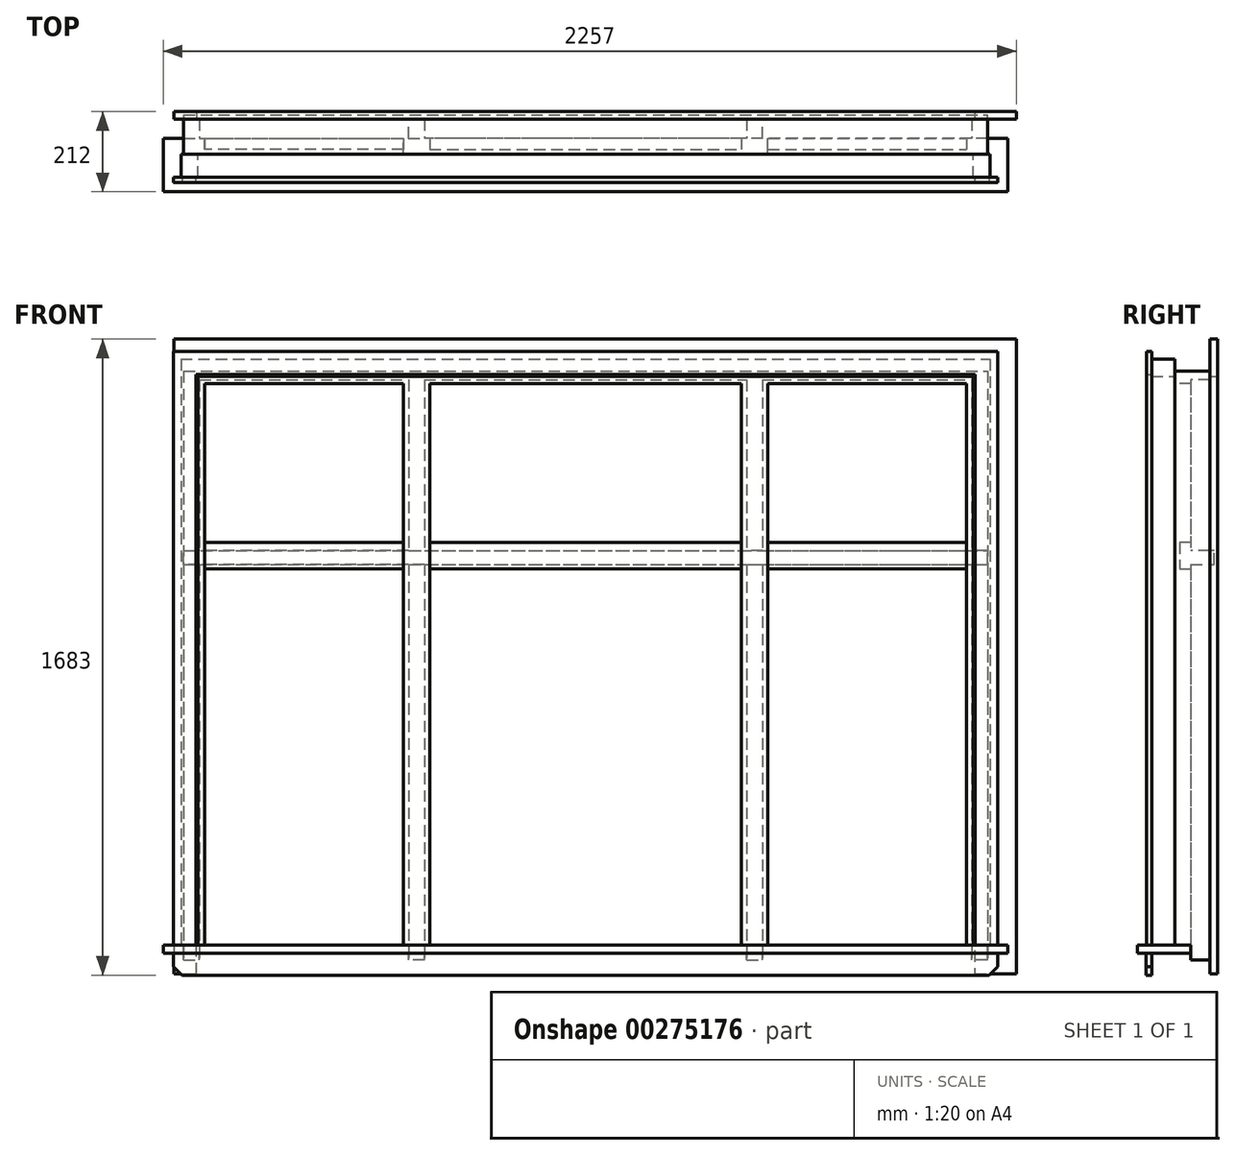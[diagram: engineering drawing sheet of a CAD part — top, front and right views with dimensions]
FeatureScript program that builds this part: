
annotation { "Feature Type Name" : "Feature", "Feature Type Description" : "" }
export const myFeature = defineFeature(function(context is Context, id is Id, definition is map)
    precondition{}
    {
        {
            var Q0;
            Q0=qCreatedBy(makeId("Top.planeOp"),FACE);
            var sketch = newSketch(context, id + "F0", { "sketchPlane" : qUnion([Q0])});
            skLineSegment(sketch, "E0", {"start": v(426.5, 0) * mm, "end": v(412.5, 0) * mm});
            skLineSegment(sketch, "E1", {"start": v(412.5, 0) * mm, "end": v(412.5, -42) * mm});
            skLineSegment(sketch, "E2", {"start": v(412.5, -42) * mm, "end": v(482.5, -42) * mm});
            skLineSegment(sketch, "E3", {"start": v(482.5, -42) * mm, "end": v(482.5, 0) * mm});
            skLineSegment(sketch, "E4", {"start": v(482.5, 0) * mm, "end": v(468.5, 0) * mm});
            skLineSegment(sketch, "E5", {"start": v(468.5, 0) * mm, "end": v(468.5, 50) * mm});
            skLineSegment(sketch, "E6", {"start": v(468.5, 50) * mm, "end": v(426.5, 50) * mm});
            skLineSegment(sketch, "E7", {"start": v(426.5, 50) * mm, "end": v(426.5, 0) * mm});
            skLineSegment(sketch, "E8", {"start": v(1007.5, 0) * mm, "end": v(1007.5, -42) * mm});
            skLineSegment(sketch, "E9", {"start": v(1007.5, -42) * mm, "end": v(1063.5, -42) * mm});
            skLineSegment(sketch, "E10", {"start": v(1063.5, -42) * mm, "end": v(1063.5, 50) * mm});
            skLineSegment(sketch, "E11", {"start": v(1063.5, 50) * mm, "end": v(1021.5, 50) * mm});
            skLineSegment(sketch, "E12", {"start": v(1021.5, 50) * mm, "end": v(1021.5, 0) * mm});
            skLineSegment(sketch, "E13", {"start": v(1021.5, 0) * mm, "end": v(1007.5, 0) * mm});
            skSolve(sketch);
        }
        {
            var Q0;
            Q0 = qSketchRegion(id + "F0", true);
            extrude(context, id + "F1", {"entities" : qUnion([Q0]), "depth" : 1485 * mm});
        }
        {
            var Q0;
            Q0=makeQuery(id+"F1.opExtrude","CAP_FACE",FACE,{"disambiguationData":[OSD([sQuery(id+"F0.wireOp",EDGE,"E8"),sQuery(id+"F0.wireOp",EDGE,"E9"),sQuery(id+"F0.wireOp",EDGE,"E10"),sQuery(id+"F0.wireOp",EDGE,"E11"),sQuery(id+"F0.wireOp",EDGE,"E12"),sQuery(id+"F0.wireOp",EDGE,"E13")])],"isStart":false});
            var sketch = newSketch(context, id + "F2", { "sketchPlane" : qUnion([Q0])});
            skLineSegment(sketch, "E14.bottom", {"start": v(1063.5, -42) * mm, "end": v(0, -42) * mm});
            skLineSegment(sketch, "E14.top", {"start": v(1063.5, 0) * mm, "end": v(0, 0) * mm});
            skLineSegment(sketch, "E14.left", {"start": v(1063.5, -42) * mm, "end": v(1063.5, 0) * mm});
            skLineSegment(sketch, "E14.right", {"start": v(0, -42) * mm, "end": v(0, 0) * mm});
            skSolve(sketch);
        }
        {
            var Q0;
            Q0 = qSketchRegion(id + "F2", true);
            extrude(context, id + "F3", {"entities" : qUnion([Q0]), "operationType" : NewBodyOperationType.ADD, "depth" : 33 * mm});
        }
        {
            var Q0;
            Q0=makeQuery(id+"F1.opExtrude","CAP_FACE",FACE,{"disambiguationData":[OSD([sQuery(id+"F0.wireOp",EDGE,"E0"),sQuery(id+"F0.wireOp",EDGE,"E1"),sQuery(id+"F0.wireOp",EDGE,"E2"),sQuery(id+"F0.wireOp",EDGE,"E3"),sQuery(id+"F0.wireOp",EDGE,"E4"),sQuery(id+"F0.wireOp",EDGE,"E5"),sQuery(id+"F0.wireOp",EDGE,"E6"),sQuery(id+"F0.wireOp",EDGE,"E7")])],"isStart":true});
            var sketch = newSketch(context, id + "F4", { "sketchPlane" : qUnion([Q0])});
            skLineSegment(sketch, "E15.bottom", {"start": v(1117.5, 0) * mm, "end": v(0, 0) * mm});
            skLineSegment(sketch, "E15.top", {"start": v(1117.5, 142) * mm, "end": v(0, 142) * mm});
            skLineSegment(sketch, "E15.left", {"start": v(1117.5, 0) * mm, "end": v(1117.5, 142) * mm});
            skLineSegment(sketch, "E15.right", {"start": v(0, 0) * mm, "end": v(0, 142) * mm});
            skSolve(sketch);
        }
        {
            var Q0;
            Q0 = qSketchRegion(id + "F4", true);
            extrude(context, id + "F5", {"entities" : qUnion([Q0]), "operationType" : NewBodyOperationType.ADD, "depth" : 22 * mm});
        }
        {
            var Q0;
            Q0=makeQuery(id+"F3.boolean.opBoolean","MERGE",FACE,{"derivedFrom":[makeQuery(id+"F1.opExtrude","SWEPT_FACE",FACE,{"disambiguationData":[OSD([sQuery(id+"F0.wireOp",EDGE,"E10")])]}),makeQuery(id+"F3.opExtrude","SWEPT_FACE",FACE,{"disambiguationData":[OSD([sQuery(id+"F2.wireOp",EDGE,"E14.left")])]})]});
            var sketch = newSketch(context, id + "F6", { "sketchPlane" : qUnion([Q0])});
            skLineSegment(sketch, "E16", {"start": v(-30, 1065) * mm, "end": v(-30, 995) * mm});
            skLineSegment(sketch, "E17", {"start": v(0, 1007) * mm, "end": v(0, 995) * mm});
            skLineSegment(sketch, "E18", {"start": v(0, 1007) * mm, "end": v(62, 1007) * mm});
            skLineSegment(sketch, "E19", {"start": v(62, 1007) * mm, "end": v(62, 1043) * mm});
            skLineSegment(sketch, "E20", {"start": v(62, 1043) * mm, "end": v(0, 1043) * mm});
            skLineSegment(sketch, "E21", {"start": v(0, 1043) * mm, "end": v(0, 1065) * mm});
            skLineSegment(sketch, "E22", {"start": v(0, 1065) * mm, "end": v(-30, 1065) * mm});
            skLineSegment(sketch, "E23", {"start": v(-30, 995) * mm, "end": v(0, 995) * mm});
            skSolve(sketch);
        }
        {
            var Q0;
            Q0 = qSketchRegion(id + "F6", true);
            var Q1;
            Q1=makeQuery(id+"F5.opExtrude","SWEPT_FACE",FACE,{"disambiguationData":[OSD([sQuery(id+"F4.wireOp",EDGE,"E15.right")])]});
            extrude(context, id + "F7", {"entities" : qUnion([Q0]), "operationType" : NewBodyOperationType.ADD, "endBound" : BoundingType.UP_TO_SURFACE, "oppositeDirection" : true, "endBoundEntityFace" : qUnion([Q1]), "depth" : 25 * mm});
        }
        {
            var Q0;
            Q0=makeQuery(id+"F3.boolean.opBoolean","MERGE",FACE,{"derivedFrom":[makeQuery(id+"F1.opExtrude","SWEPT_FACE",FACE,{"disambiguationData":[OSD([sQuery(id+"F0.wireOp",EDGE,"E2")])]}),makeQuery(id+"F1.opExtrude","SWEPT_FACE",FACE,{"disambiguationData":[OSD([sQuery(id+"F0.wireOp",EDGE,"E9")])]}),makeQuery(id+"F3.opExtrude","SWEPT_FACE",FACE,{"disambiguationData":[OSD([sQuery(id+"F2.wireOp",EDGE,"E14.bottom")])]})]});
            var sketch = newSketch(context, id + "F8", { "sketchPlane" : qUnion([Q0])});
            skLineSegment(sketch, "E24", {"start": v(1025.5, 0) * mm, "end": v(1025.5, 1505) * mm});
            skLineSegment(sketch, "E25", {"start": v(1025.5, 1505) * mm, "end": v(0, 1505) * mm});
            skPoint(sketch, "E25.endSnap0", {"position": v(0, 1501.5) * mm});
            skLineSegment(sketch, "E26", {"start": v(0, 1505) * mm, "end": v(0, 1550) * mm});
            skLineSegment(sketch, "E27", {"start": v(0, 1550) * mm, "end": v(1070.5, 1550) * mm});
            skLineSegment(sketch, "E28", {"start": v(1070.5, 1550) * mm, "end": v(1070.5, 0) * mm});
            skLineSegment(sketch, "E29", {"start": v(1070.5, 0) * mm, "end": v(1025.5, 0) * mm});
            skSolve(sketch);
        }
        {
            var Q0;
            Q0 = qSketchRegion(id + "F8", true);
            extrude(context, id + "F9", {"entities" : qUnion([Q0]), "operationType" : NewBodyOperationType.ADD, "depth" : 62 * mm});
        }
        {
            var Q0;
            Q0=makeQuery(id+"F9.opExtrude","CAP_FACE",FACE,{"disambiguationData":[OSD([sQuery(id+"F8.wireOp",EDGE,"E24"),sQuery(id+"F8.wireOp",EDGE,"E25"),sQuery(id+"F8.wireOp",EDGE,"E26"),sQuery(id+"F8.wireOp",EDGE,"E27"),sQuery(id+"F8.wireOp",EDGE,"E28"),sQuery(id+"F8.wireOp",EDGE,"E29")])],"isStart":false});
            var sketch = newSketch(context, id + "F10", { "sketchPlane" : qUnion([Q0])});
            skLineSegment(sketch, "E30", {"start": v(1030.5, 0) * mm, "end": v(1090.5, 0) * mm});
            skPoint(sketch, "E30.endSnap0", {"position": v(1048, 0) * mm});
            skLineSegment(sketch, "E31", {"start": v(1030.5, 0) * mm, "end": v(1030.5, 1510) * mm});
            skLineSegment(sketch, "E32", {"start": v(1030.5, 1510) * mm, "end": v(0, 1510) * mm});
            skLineSegment(sketch, "E33", {"start": v(0, 1510) * mm, "end": v(0, 1570) * mm});
            skPoint(sketch, "E33.endSnap0", {"position": v(0, 1527.5) * mm});
            skLineSegment(sketch, "E34", {"start": v(0, 1570) * mm, "end": v(1090.5, 1570) * mm});
            skLineSegment(sketch, "E35", {"start": v(1090.5, 1570) * mm, "end": v(1090.5, 0) * mm});
            skSolve(sketch);
        }
        {
            var Q0;
            Q0 = qSketchRegion(id + "F10", true);
            extrude(context, id + "F11", {"entities" : qUnion([Q0]), "operationType" : NewBodyOperationType.ADD, "depth" : 13 * mm});
        }
        {
            var Q0;
            Q0=makeQuery(id+"F5.opExtrude","SWEPT_FACE",FACE,{"disambiguationData":[OSD([sQuery(id+"F4.wireOp",EDGE,"E15.top")])]});
            cPlane(context, id + "F12", {"entities" : qUnion([Q0]), "cplaneType" : CPlaneType.OFFSET, "offset" : 23 * mm, "oppositeDirection" : true, "width" : 150 * mm, "height" : 150 * mm});
        }
        {
            var Q0;
            Q0=qCreatedBy(id+"F12.planeOp",FACE);
            var sketch = newSketch(context, id + "F13", { "sketchPlane" : qUnion([Q0])});
            skLineSegment(sketch, "E36", {"start": v(1090.5, -22) * mm, "end": v(1090.5, -57) * mm});
            skLineSegment(sketch, "E37", {"start": v(1090.5, -57) * mm, "end": v(1067.5, -80) * mm});
            skLineSegment(sketch, "E38", {"start": v(1067.5, -80) * mm, "end": v(0, -80) * mm});
            skLineSegment(sketch, "E39", {"start": v(0, -80) * mm, "end": v(0, -22) * mm});
            skLineSegment(sketch, "E40", {"start": v(0, -22) * mm, "end": v(1090.5, -22) * mm});
            skSolve(sketch);
        }
        {
            var Q0;
            Q0 = qSketchRegion(id + "F13", true);
            extrude(context, id + "F14", {"entities" : qUnion([Q0]), "operationType" : NewBodyOperationType.ADD, "oppositeDirection" : true, "depth" : 15 * mm});
        }
        {
            var Q0;
            Q0=makeQuery(id+"F7.boolean.opBoolean","MERGE",FACE,{"derivedFrom":[makeQuery(id+"F5.boolean.opBoolean","MERGE",FACE,{"derivedFrom":[makeQuery(id+"F3.boolean.opBoolean","MERGE",FACE,{"derivedFrom":[makeQuery(id+"F1.opExtrude","SWEPT_FACE",FACE,{"disambiguationData":[OSD([sQuery(id+"F0.wireOp",EDGE,"E0")])]}),makeQuery(id+"F1.opExtrude","SWEPT_FACE",FACE,{"disambiguationData":[OSD([sQuery(id+"F0.wireOp",EDGE,"E4")])]}),makeQuery(id+"F1.opExtrude","SWEPT_FACE",FACE,{"disambiguationData":[OSD([sQuery(id+"F0.wireOp",EDGE,"E13")])]}),makeQuery(id+"F3.opExtrude","SWEPT_FACE",FACE,{"disambiguationData":[OSD([sQuery(id+"F2.wireOp",EDGE,"E14.top")])]})]}),makeQuery(id+"F5.opExtrude","SWEPT_FACE",FACE,{"disambiguationData":[OSD([sQuery(id+"F4.wireOp",EDGE,"E15.bottom")])]})]}),makeQuery(id+"F7.opExtrude","SWEPT_FACE",FACE,{"disambiguationData":[OSD([sQuery(id+"F6.wireOp",EDGE,"E21")])]})]});
            var sketch = newSketch(context, id + "F15", { "sketchPlane" : qUnion([Q0])});
            skLineSegment(sketch, "E41", {"start": v(-1063.5, 1485) * mm, "end": v(-1063.5, 1518) * mm});
            skLineSegment(sketch, "E42", {"start": v(-1063.5, 1518) * mm, "end": v(0, 1518) * mm});
            skLineSegment(sketch, "E43", {"start": v(0, 1518) * mm, "end": v(0, 1495) * mm});
            skLineSegment(sketch, "E44", {"start": v(0, 1495) * mm, "end": v(-426.5, 1495) * mm});
            skLineSegment(sketch, "E45", {"start": v(-426.5, 1495) * mm, "end": v(-426.5, 1485) * mm});
            skLineSegment(sketch, "E46", {"start": v(-426.5, 1485) * mm, "end": v(-468.5, 1485) * mm});
            skLineSegment(sketch, "E47", {"start": v(-468.5, 1485) * mm, "end": v(-468.5, 1495) * mm});
            skLineSegment(sketch, "E48", {"start": v(-468.5, 1495) * mm, "end": v(-1021.5, 1495) * mm});
            skLineSegment(sketch, "E49", {"start": v(-1021.5, 1495) * mm, "end": v(-1021.5, 1485) * mm});
            skLineSegment(sketch, "E50", {"start": v(-1021.5, 1485) * mm, "end": v(-1063.5, 1485) * mm});
            skSolve(sketch);
        }
        {
            var Q0;
            Q0 = qSketchRegion(id + "F15", true);
            var Q1;
            {var subQ1=sQuery(id+"F0.wireOp",EDGE,"E6");Q1=makeQuery(id+"F7.boolean.opBoolean","SPLIT",FACE,{"disambiguationData":[TD([makeQuery(id+"F7.opExtrude","SWEPT_FACE",FACE,{"disambiguationData":[OSD([sQuery(id+"F6.wireOp",EDGE,"E20")])]})])],"derivedFrom":makeQuery(id+"F1.opExtrude","SWEPT_FACE",FACE,{"disambiguationData":[OSD([subQ1])]})});}
            extrude(context, id + "F16", {"entities" : qUnion([Q0]), "operationType" : NewBodyOperationType.ADD, "endBound" : BoundingType.UP_TO_SURFACE, "endBoundEntityFace" : qUnion([Q1]), "depth" : 25 * mm});
        }
        {
            var Q0;
            Q0=makeQuery(id+"F1.opExtrude","CAP_FACE",FACE,{"disambiguationData":[OSD([sQuery(id+"F0.wireOp",EDGE,"E8"),sQuery(id+"F0.wireOp",EDGE,"E9"),sQuery(id+"F0.wireOp",EDGE,"E10"),sQuery(id+"F0.wireOp",EDGE,"E11"),sQuery(id+"F0.wireOp",EDGE,"E12"),sQuery(id+"F0.wireOp",EDGE,"E13")])],"isStart":true});
            var sketch = newSketch(context, id + "F17", { "sketchPlane" : qUnion([Q0])});
            skLineSegment(sketch, "E51", {"start": v(1063.5, 0) * mm, "end": v(1063.5, -50) * mm});
            skLineSegment(sketch, "E52", {"start": v(1063.5, -50) * mm, "end": v(1021.5, -50) * mm});
            skLineSegment(sketch, "E53", {"start": v(1021.5, -50) * mm, "end": v(1021.5, 0) * mm});
            skLineSegment(sketch, "E54", {"start": v(1021.5, 0) * mm, "end": v(1063.5, 0) * mm});
            skLineSegment(sketch, "E55", {"start": v(426.5, -50) * mm, "end": v(468.5, -50) * mm});
            skLineSegment(sketch, "E56", {"start": v(468.5, -50) * mm, "end": v(468.5, 0) * mm});
            skLineSegment(sketch, "E57", {"start": v(468.5, 0) * mm, "end": v(426.5, 0) * mm});
            skLineSegment(sketch, "E58", {"start": v(426.5, 0) * mm, "end": v(426.5, -50) * mm});
            skSolve(sketch);
        }
        {
            var Q0;
            Q0=makeQuery(id+"F17.imprint","IMPRINT",FACE,{"disambiguationData":[TD([[makeQuery(id+"F17.imprint","IMPRINT",EDGE,{"derivedFrom":sQuery(id+"F17.wireOp",EDGE,"E55")}),1.0]])]});
            var Q1;
            Q1=makeQuery(id+"F17.imprint","IMPRINT",FACE,{"disambiguationData":[TD([[makeQuery(id+"F17.imprint","IMPRINT",EDGE,{"derivedFrom":sQuery(id+"F17.wireOp",EDGE,"E51")}),-1.0]])]});
            extrude(context, id + "F18", {"entities" : qUnion([Q0, Q1]), "operationType" : NewBodyOperationType.ADD, "depth" : 40 * mm});
        }
        {
            var Q0;
            Q0=makeQuery(id+"F1.opExtrude","SWEPT_BODY",BODY,{"disambiguationData":[OSD([sQuery(id+"F0.wireOp",EDGE,"E0"),sQuery(id+"F0.wireOp",EDGE,"E1"),sQuery(id+"F0.wireOp",EDGE,"E2"),sQuery(id+"F0.wireOp",EDGE,"E3"),sQuery(id+"F0.wireOp",EDGE,"E4"),sQuery(id+"F0.wireOp",EDGE,"E5"),sQuery(id+"F0.wireOp",EDGE,"E6"),sQuery(id+"F0.wireOp",EDGE,"E7")])]});
            var Q1;
            Q1=qCreatedBy(makeId("Right.planeOp"),FACE);
            mirror(context, id + "F19", {"operationType" : NewBodyOperationType.ADD, "entities" : qUnion([Q0]), "mirrorPlane" : qUnion([Q1])});
        }
        {
            var Q0;
            {var subQ2=sQuery(id+"F0.wireOp",EDGE,"E11");var subQ3=sQuery(id+"F6.wireOp",EDGE,"E20");var subQ4=makeQuery(id+"F7.opExtrude","SWEPT_FACE",FACE,{"disambiguationData":[OSD([subQ3])]});var subQ6=sQuery(id+"F0.wireOp",EDGE,"E6");var subQ8=makeQuery(id+"F16.boolean.opBoolean","MERGE",FACE,{"derivedFrom":[makeQuery(id+"F7.boolean.opBoolean","SPLIT",FACE,{"disambiguationData":[TD([subQ4])],"derivedFrom":makeQuery(id+"F1.opExtrude","SWEPT_FACE",FACE,{"disambiguationData":[OSD([subQ6])]})}),makeQuery(id+"F7.boolean.opBoolean","SPLIT",FACE,{"disambiguationData":[TD([subQ4])],"derivedFrom":makeQuery(id+"F1.opExtrude","SWEPT_FACE",FACE,{"disambiguationData":[OSD([subQ2])]})}),makeQuery(id+"F16.opExtrude","CAP_FACE",FACE,{"disambiguationData":[OSD([sQuery(id+"F15.wireOp",EDGE,"E41"),sQuery(id+"F15.wireOp",EDGE,"E42"),sQuery(id+"F15.wireOp",EDGE,"E43"),sQuery(id+"F15.wireOp",EDGE,"E44"),sQuery(id+"F15.wireOp",EDGE,"E45"),sQuery(id+"F15.wireOp",EDGE,"E46"),sQuery(id+"F15.wireOp",EDGE,"E47"),sQuery(id+"F15.wireOp",EDGE,"E48"),sQuery(id+"F15.wireOp",EDGE,"E49"),sQuery(id+"F15.wireOp",EDGE,"E50")])],"isStart":false})]});Q0=makeQuery(id+"F19.boolean.opBoolean","MERGE",FACE,{"derivedFrom":[subQ8,makeQuery(id+"F19.opPattern","COPY",FACE,{"derivedFrom":subQ8,"instanceName":"1"})]});}
            var sketch = newSketch(context, id + "F20", { "sketchPlane" : qUnion([Q0])});
            skLineSegment(sketch, "E59", {"start": v(-1029.5, 1503) * mm, "end": v(-1029.5, -77) * mm});
            skLineSegment(sketch, "E60", {"start": v(-1029.5, -77) * mm, "end": v(-1139.5, -77) * mm});
            skLineSegment(sketch, "E61", {"start": v(-1139.5, -77) * mm, "end": v(-1139.5, 1603) * mm});
            skLineSegment(sketch, "E62", {"start": v(-1139.5, 1603) * mm, "end": v(1089.5, 1603) * mm});
            skLineSegment(sketch, "E63", {"start": v(1089.5, 1603) * mm, "end": v(1089.5, -77) * mm});
            skLineSegment(sketch, "E64", {"start": v(1089.5, -77) * mm, "end": v(1029.5, -77) * mm});
            skLineSegment(sketch, "E65", {"start": v(1029.5, -77) * mm, "end": v(1029.5, 1503) * mm});
            skLineSegment(sketch, "E66", {"start": v(1029.5, 1503) * mm, "end": v(-1029.5, 1503) * mm});
            skSolve(sketch);
        }
        {
            var Q0;
            Q0 = qSketchRegion(id + "F20", true);
            extrude(context, id + "F21", {"entities" : qUnion([Q0]), "depth" : 20 * mm});
        }
    });
